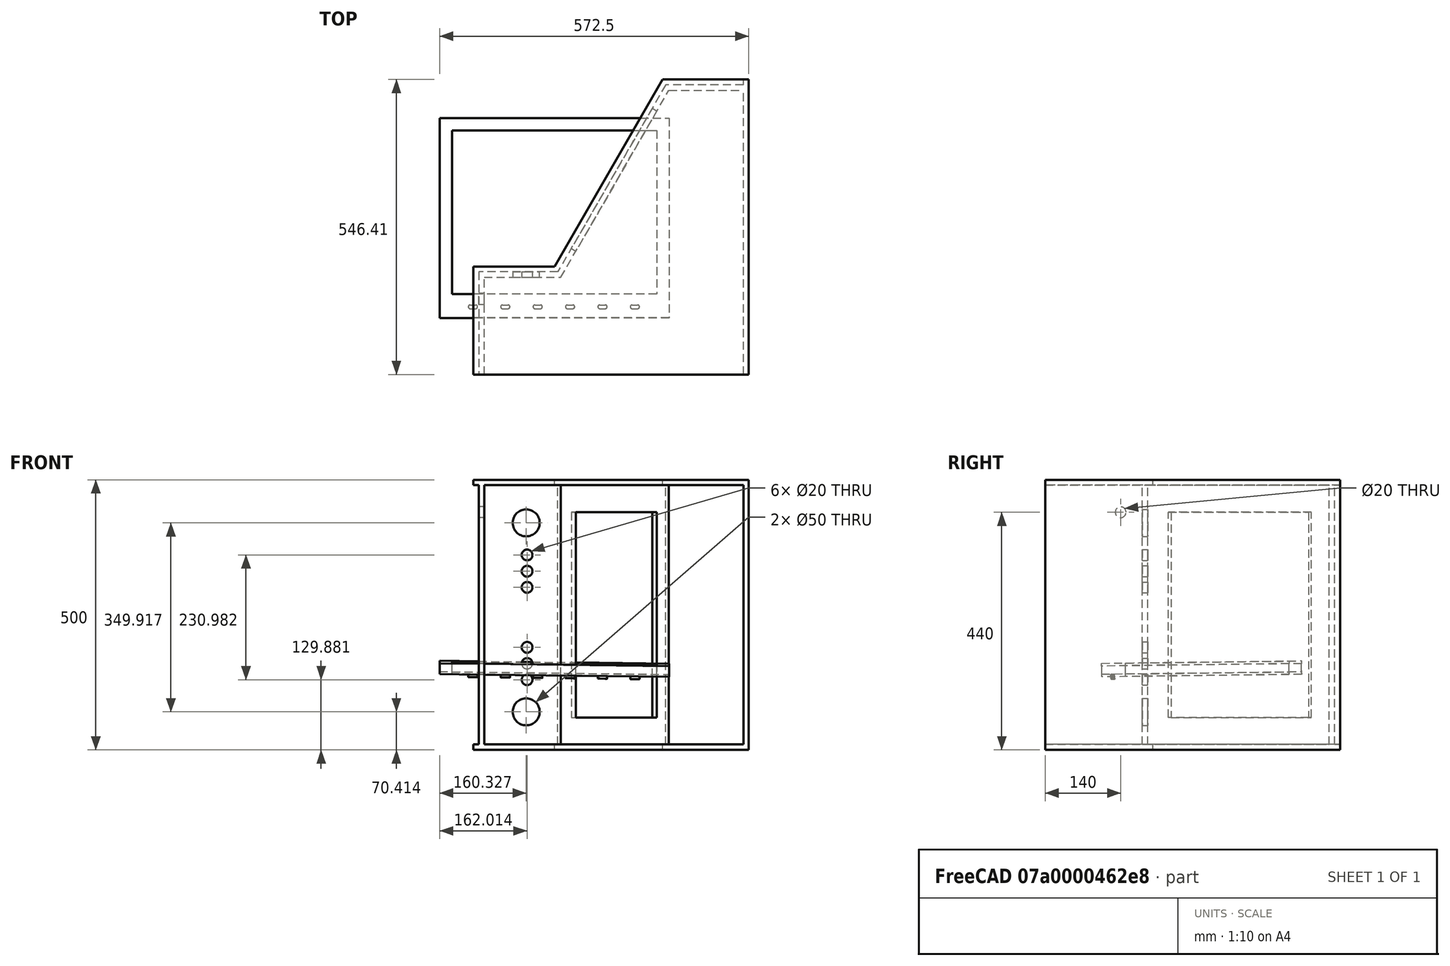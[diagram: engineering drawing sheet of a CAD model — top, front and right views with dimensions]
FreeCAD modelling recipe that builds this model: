
FCSTD DOCUMENT  (FreeCAD 0.18R16131 (Git))
Label: arcade
License: All rights reserved
LicenseURL: http://en.wikipedia.org/wiki/All_rights_reserved
objects: Sketcher::SketchObject×9, TechDraw::DrawViewDimension×7, PartDesign::Pad×5, PartDesign::Plane×3, PartDesign::Pocket×3, TechDraw::DrawViewPart×3, PartDesign::LinearPattern×2, PartDesign::Body×2, PartDesign::Mirrored×1, TechDraw::DrawSVGTemplate×1, TechDraw::DrawPage×1
note: 33 computed .brp shape members not serialized (recipe doc carries the construction recipe); baked Part::Feature solids carry a one-line shape summary decoded from their .brp

FEATURE [Sketcher::SketchObject] Sketch  label="coteGauche"
  MapMode = 5
  Support = -> [XY_Plane]
  sketch-geometry (6):
    g0: LineSegment StartX=-500 StartY=200 StartZ=0 EndX=-500 EndY=0 EndZ=0
    g1: LineSegment StartX=-500 StartY=0 StartZ=0 EndX=0 EndY=0 EndZ=0
    g2: LineSegment StartX=0 StartY=0 StartZ=0 EndX=0 EndY=546.41 EndZ=0
    g3: LineSegment StartX=0 StartY=546.41 StartZ=0 EndX=-149.507 EndY=546.41 EndZ=0
    g4: LineSegment StartX=-149.507 StartY=546.41 StartZ=0 EndX=-349.507 EndY=200 EndZ=0
    g5: LineSegment StartX=-349.507 StartY=200 StartZ=0 EndX=-500 EndY=200 EndZ=0
  constraints (16):
    c: Vertical(g0)
    c: Coincident(g0,g1)
    c: Horizontal(g1)
    c: Coincident(g1,g2)
    c: Vertical(g2)
    c: Coincident(g2,g3)
    c: Horizontal(g3)
    c: Coincident(g3,g4)
    c: Coincident(g5,g0)
    c: DistanceX(g1,g1) = 500
    c: DistanceY(g0,g0) = 200
    c: Horizontal(g5)
    c: Coincident(g4,g5)
    c: Coincident(g1,g-1)
    c: Angle(g4,g3) = 2.0944
    c: Distance(g4) = 400
FEATURE [PartDesign::Pad] Pad
  Length = 10
  Length2 = 100
  Profile = -> Sketch
  Type = 0
FEATURE [Sketcher::SketchObject] Sketch001
  ExternalGeometry = -> [Pad]
  MapMode = 5
  Placement = pos=(0,0,0) rot=(0.57735,0.57735,0.57735;2.0944rad)
  Support = -> [Pad]
  sketch-geometry (4):
    g0: LineSegment StartX=522.259 StartY=0 StartZ=0 EndX=-24.8181 EndY=0 EndZ=0
    g1: LineSegment StartX=-24.8181 StartY=0 StartZ=0 EndX=-24.8181 EndY=10 EndZ=0
    g2: LineSegment StartX=-24.8181 StartY=10 StartZ=0 EndX=522.259 EndY=10 EndZ=0
    g3: LineSegment StartX=522.259 StartY=10 StartZ=0 EndX=522.259 EndY=0 EndZ=0
  constraints (10):
    c: Coincident(g0,g1)
    c: Coincident(g1,g2)
    c: Coincident(g2,g3)
    c: Coincident(g3,g0)
    c: Horizontal(g0)
    c: Horizontal(g2)
    c: Vertical(g1)
    c: Vertical(g3)
    c: DistanceY(g0,g-3) = 10
    c: DistanceY(g-4,g2) = 10
FEATURE [Sketcher::SketchObject] Sketch002  label="arriere"
  ExternalGeometry = -> [Sketch]
  MapMode = 5
  Placement = pos=(0,0,0) rot=(0.57735,0.57735,0.57735;2.0944rad)
  Support = -> [YZ_Plane]
  sketch-geometry (4):
    g0: LineSegment StartX=0 StartY=0 StartZ=0 EndX=546.41 EndY=1.386e-13 EndZ=0
    g1: LineSegment StartX=546.41 StartY=1.386e-13 StartZ=0 EndX=546.41 EndY=500 EndZ=0
    g2: LineSegment StartX=546.41 StartY=500 StartZ=0 EndX=0 EndY=500 EndZ=0
    g3: LineSegment StartX=0 StartY=500 StartZ=0 EndX=0 EndY=0 EndZ=0
  constraints (10):
    c: Coincident(g0,g1)
    c: Coincident(g1,g2)
    c: Coincident(g2,g3)
    c: Coincident(g3,g0)
    c: Horizontal(g2)
    c: Vertical(g1)
    c: Vertical(g3)
    c: Coincident(g0,g-1)
    c: Coincident(g0,g-3)
    c: DistanceY(g1,g1) = 500
FEATURE [PartDesign::Pad] Pad001
  BaseFeature = -> Pad
  Length = 10
  Length2 = 100
  Profile = -> Sketch002
  Type = 0
FEATURE [PartDesign::LinearPattern] LinearPattern  label="coteDroit"
  BaseFeature = -> Pad001
  Direction = -> Z_Axis
  Length = 490
  Occurrences = 2
  Originals = -> [Pad]
FEATURE [Sketcher::SketchObject] Sketch003  label="Interieur"
  ExternalGeometry = -> [Sketch]
  MapMode = 5
  Support = -> [XY_Plane]
  sketch-geometry (14):
    g0: LineSegment StartX=-490 StartY=190 StartZ=0 EndX=-343.734 EndY=190 EndZ=0
    g1: LineSegment StartX=-343.734 StartY=190 StartZ=0 EndX=-143.734 EndY=536.41 EndZ=0
    g2: LineSegment StartX=-143.734 StartY=536.41 StartZ=0 EndX=0 EndY=536.41 EndZ=0
    g3: LineSegment StartX=0 StartY=536.41 StartZ=0 EndX=0 EndY=526.41 EndZ=0
    g4: LineSegment StartX=0 StartY=526.41 StartZ=0 EndX=-137.96 EndY=526.41 EndZ=0
    g5: LineSegment StartX=-137.96 StartY=526.41 StartZ=0 EndX=-337.96 EndY=180 EndZ=0
    g6: LineSegment StartX=-337.96 StartY=180 StartZ=0 EndX=-480 EndY=180 EndZ=0
    g7: LineSegment StartX=-480 StartY=180 StartZ=0 EndX=-480 EndY=0 EndZ=0
    g8: LineSegment StartX=-480 StartY=0 StartZ=0 EndX=-490 EndY=0 EndZ=0
    g9: LineSegment StartX=-490 StartY=0 StartZ=0 EndX=-490 EndY=190 EndZ=0
    g10: LineSegment [constr] StartX=-310.722 StartY=318.165 StartZ=0 EndX=-188.581 EndY=247.647 EndZ=0
    g11: GeomPoint X=-279.984 Y=300.419 Z=0
    g12: GeomPoint X=-271.323 Y=295.419 Z=0
    g13: GeomPoint X=-288.644 Y=305.419 Z=0
  constraints (37):
    c: Horizontal(g0)
    c: Coincident(g0,g1)
    c: Coincident(g1,g2)
    c: PointOnObject(g2,g-2)
    c: Horizontal(g2)
    c: Coincident(g2,g3)
    c: Coincident(g3,g4)
    c: Horizontal(g4)
    c: Coincident(g4,g5)
    c: Coincident(g5,g6)
    c: Horizontal(g6)
    c: Coincident(g6,g7)
    c: PointOnObject(g7,g-1)
    c: Vertical(g7)
    c: Coincident(g7,g8)
    c: PointOnObject(g8,g-1)
    c: Coincident(g8,g9)
    c: Vertical(g9)
    c: Coincident(g9,g0)
    c: DistanceX(g8,g7) = 10
    c: DistanceY(g6,g0) = 10
    c: Vertical(g3)
    c: DistanceY(g3,g2) = 10
    c: Parallel(g1,g5)
    c: Parallel(g-4,g1)
    c: DistanceY(g0,g-3) = 10
    c: DistanceY(g1,g-4) = 10
    c: Perpendicular(g5,g10)
    c: PointOnObject(g11,g1)
    c: PointOnObject(g12,g10)
    c: PointOnObject(g12,g5)
    c: PointOnObject(g11,g10)
    c: Distance(g11,g12) = 10
    c: PointOnObject(g13,g10)
    c: PointOnObject(g13,g-4)
    c: Distance(g13,g11) = 10
    c: DistanceX(g-3,g8) = 10
FEATURE [PartDesign::Pad] Pad002
  BaseFeature = -> LinearPattern
  Length = 490
  Length2 = 100
  Profile = -> Sketch003
  Type = 0
FEATURE [PartDesign::Plane] DatumPlane
  Length = 859.471
  MapMode = 5
  Placement = pos=(-340.073,196.341,0) rot=(-0.377964,0.654654,0.654654;3.86433rad)
  ResizeMode = 0
  Support = -> [Pad002]
  Width = 632.605
FEATURE [Sketcher::SketchObject] Sketch004  label="ecran"
  ExternalGeometry = -> [Pad002,Sketch003]
  MapMode = 5
  Placement = pos=(-340.073,196.341,0) rot=(-0.377964,0.654654,0.654654;3.86433rad)
  Support = -> [DatumPlane]
  sketch-geometry (5):
    g0: LineSegment StartX=-342.678 StartY=440 StartZ=0 EndX=-42.6779 EndY=440 EndZ=0
    g1: LineSegment StartX=-42.6779 StartY=440 StartZ=0 EndX=-42.6779 EndY=60 EndZ=0
    g2: LineSegment StartX=-42.6779 StartY=60 StartZ=0 EndX=-342.678 EndY=60 EndZ=0
    g3: LineSegment StartX=-342.678 StartY=60 StartZ=0 EndX=-342.678 EndY=440 EndZ=0
    g4: LineSegment [constr] StartX=7.32214 StartY=-5e-16 StartZ=0 EndX=7.32214 EndY=590 EndZ=0
  constraints (14):
    c: Coincident(g0,g1)
    c: Coincident(g1,g2)
    c: Coincident(g2,g3)
    c: Coincident(g3,g0)
    c: Horizontal(g0)
    c: Horizontal(g2)
    c: Vertical(g1)
    c: Vertical(g3)
    c: Distance(g0,g-5) = 50
    c: Distance(g1,g-7) = 50
    c: DistanceY(g0,g-5) = 50
    c: Coincident(g4,g-8)
    c: Vertical(g4)
    c: DistanceX(g1,g4) = 50
FEATURE [PartDesign::Pocket] Pocket
  BaseFeature = -> Pad002
  Length = 25
  Length2 = 100
  Profile = -> Sketch004
  Type = 0
FEATURE [PartDesign::Plane] DatumPlane001
  Length = 612
  MapMode = 5
  Placement = pos=(0,190,0) rot=(0,0.707107,0.707107;3.14159rad)
  ResizeMode = 0
  Support = -> [Pocket]
  Width = 612
FEATURE [Sketcher::SketchObject] Sketch005  label="manettes"
  ExternalGeometry = -> [Pocket]
  MapMode = 5
  Placement = pos=(0,190,0) rot=(0,0.707107,0.707107;3.14159rad)
  Support = -> [DatumPlane001]
  sketch-geometry (8):
    g0: LineSegment [constr] StartX=400.486 StartY=-101.961 StartZ=0 EndX=400.486 EndY=591.027 EndZ=0
    g1: LineSegment [constr] StartX=285.859 StartY=245.372 StartZ=0 EndX=534.194 EndY=245.372 EndZ=0
    g2: GeomPoint X=400.486 Y=10 Z=0
    g3: GeomPoint X=400.486 Y=490 Z=0
    g4: Circle CenterX=402.174 CenterY=70.4137 CenterZ=0 NormalX=0 NormalY=0 NormalZ=1 AngleXU=0 Radius=25
    g5: Circle CenterX=400.486 CenterY=129.881 CenterZ=0 NormalX=0 NormalY=0 NormalZ=1 AngleXU=0 Radius=10
    g6: Circle CenterX=400.486 CenterY=159.881 CenterZ=0 NormalX=0 NormalY=0 NormalZ=1 AngleXU=0 Radius=10
    g7: Circle CenterX=400.486 CenterY=189.881 CenterZ=0 NormalX=0 NormalY=0 NormalZ=1 AngleXU=0 Radius=10
  constraints (15):
    c: Vertical(g0)
    c: Horizontal(g1)
    c: PointOnObject(g2,g0)
    c: PointOnObject(g3,g0)
    c: PointOnObject(g2,g-5)
    c: PointOnObject(g3,g-6)
    c: Radius(g4) = 25
    c: PointOnObject(g5,g0)
    c: PointOnObject(g6,g0)
    c: PointOnObject(g7,g0)
    c: Radius(g5) = 10
    c: Radius(g6) = 10
    c: Radius(g7) = 10
    c: DistanceY(g5,g6) = 30
    c: DistanceY(g6,g7) = 30
FEATURE [PartDesign::Pocket] Pocket001
  BaseFeature = -> Pocket
  Length = 20
  Length2 = 100
  Profile = -> Sketch005
  Type = 1
FEATURE [PartDesign::Mirrored] Mirrored
  BaseFeature = -> Pocket001
  MirrorPlane = -> Sketch005 [Axis1]
  Originals = -> [Pocket001]
FEATURE [PartDesign::Plane] DatumPlane002
  Length = 662.95
  MapMode = 5
  Placement = pos=(-490,0,0) rot=(0.57735,-0.57735,-0.57735;2.0944rad)
  ResizeMode = 0
  Support = -> [Mirrored]
  Width = 616.54
FEATURE [Sketcher::SketchObject] Sketch006
  ExternalGeometry = -> [Mirrored]
  MapMode = 5
  Placement = pos=(-490,0,0) rot=(0.57735,-0.57735,-0.57735;2.0944rad)
  Support = -> [DatumPlane002]
  sketch-geometry (1):
    g0: Circle CenterX=-140 CenterY=440 CenterZ=0 NormalX=0 NormalY=0 NormalZ=1 AngleXU=0 Radius=10
  constraints (1):
    c: Radius(g0) = 10
FEATURE [PartDesign::Pocket] Pocket002
  BaseFeature = -> Mirrored
  Length = 20
  Length2 = 100
  Profile = -> Sketch006
  Type = 0
FEATURE [PartDesign::Body] Body  label="socle"
  Group = -> [Sketch,Pad,Sketch001,Sketch002,Pad001,LinearPattern,Sketch003,Pad002,DatumPlane,Sketch004,Pocket,DatumPlane001,Sketch005,Pocket001,Mirrored,DatumPlane002,Sketch006,Pocket002]
  Origin = -> Origin
  Tip = -> Pocket002
FEATURE [TechDraw::DrawSVGTemplate] Template
  EditableTexts = Designed_by_Name=Designed by Name; Drawing_number=Drawing number; FC-Date=Date; FC-SC=Scale; FC-SH=Sheet; FC-Title=Title; Subtitle=Subtitle; Weight=Weight
  Height = 210
  Orientation = 1
  Width = 297
FEATURE [TechDraw::DrawViewPart] View  label="3d"
  CoarseView = true
  Direction = (-0.678,0.458,0.575)
  Focus = 1000
  HardHidden = false
  IsoCount = 0
  IsoHidden = false
  IsoVisible = false
  LockPosition = false
  Perspective = false
  Rotation = 91
  Scale = 0.1
  ScaleType = 2
  SeamHidden = false
  SeamVisible = false
  SmoothHidden = false
  SmoothVisible = false
  Source = -> [Pocket002]
  X = 217.489
  Y = 140.455
FEATURE [TechDraw::DrawViewPart] View002  label="cote"
  CoarseView = false
  Direction = (0,0,1)
  Focus = 100
  HardHidden = false
  IsoCount = 0
  IsoHidden = false
  IsoVisible = false
  LockPosition = false
  Perspective = false
  Rotation = 0
  Scale = 0.1
  ScaleType = 2
  SeamHidden = false
  SeamVisible = false
  SmoothHidden = false
  SmoothVisible = false
  Source = -> [Pad]
  X = 52.6486
  Y = 136.95
FEATURE [TechDraw::DrawViewPart] View003  label="arriere001"
  CoarseView = false
  Direction = (1,0,0)
  Focus = 100
  HardHidden = false
  IsoCount = 0
  IsoHidden = false
  IsoVisible = false
  LockPosition = false
  Perspective = false
  Rotation = 0
  Scale = 0.1
  ScaleType = 0
  SeamHidden = false
  SeamVisible = false
  SmoothHidden = false
  SmoothVisible = false
  Source = -> [Pad001]
  X = 124.047
  Y = 136.884
FEATURE [TechDraw::DrawViewDimension] Dimension  label="profondeur"
  Arbitrary = false
  FormatSpec = %.2f
  LockPosition = false
  MeasureType = 1
  OverTolerance = 0.05
  References2D = -> [View002]
  Rotation = 0
  ScaleType = 0
  Type = 1
  UnderTolerance = 0
  X = 2.73693
  Y = -44.1616
FEATURE [TechDraw::DrawViewDimension] Dimension001  label="hauteur"
  Arbitrary = false
  FormatSpec = %.2f
  LockPosition = false
  MeasureType = 1
  OverTolerance = 0
  References2D = -> [View002]
  Rotation = 0
  ScaleType = 0
  Type = 2
  UnderTolerance = 0
  X = 29.57
  Y = -0.794788
FEATURE [TechDraw::DrawViewDimension] Dimension002
  Arbitrary = false
  FormatSpec = %.2f
  LockPosition = false
  MeasureType = 1
  OverTolerance = 0
  References2D = -> [View002]
  Rotation = 0
  ScaleType = 0
  Type = 2
  UnderTolerance = 0
  X = -34.7362
  Y = -12.8143
FEATURE [TechDraw::DrawViewDimension] Dimension003
  Arbitrary = false
  FormatSpec = %.2f
  LockPosition = false
  MeasureType = 1
  OverTolerance = 0
  References2D = -> [View002]
  Rotation = 0
  ScaleType = 0
  Type = 1
  UnderTolerance = 0
  X = -14.3386
  Y = 15.8632
FEATURE [TechDraw::DrawViewDimension] Dimension004  label="largeur"
  Arbitrary = false
  FormatSpec = %.2f
  LockPosition = false
  MeasureType = 1
  OverTolerance = 0
  References2D = -> [View003]
  Rotation = 0
  ScaleType = 0
  Type = 1
  UnderTolerance = 0
  X = -3.88903
  Y = -43.1793
FEATURE [TechDraw::DrawViewDimension] Dimension005
  Arbitrary = false
  FormatSpec = %.2f
  LockPosition = false
  MeasureType = 1
  OverTolerance = 0
  References2D = -> [View002]
  Rotation = 0
  ScaleType = 0
  Type = 1
  UnderTolerance = 0
  X = 20.3151
  Y = 38.9088
FEATURE [TechDraw::DrawViewDimension] Dimension006
  Arbitrary = false
  FormatSpec = %.2f
  LockPosition = false
  MeasureType = 0
  OverTolerance = 0
  References2D = -> [View]
  References3D = -> [Sketch]
  Rotation = 0
  ScaleType = 0
  Type = 0
  UnderTolerance = 0
  X = 38.925
  Y = -38.1835
FEATURE [TechDraw::DrawPage] Page
  KeepUpdated = true
  ProjectionType = 0
  Template = -> Template
  Views = -> [View,View002,View003,Dimension,Dimension001,Dimension002,Dimension003,Dimension004,Dimension005,Dimension006]
FEATURE [Sketcher::SketchObject] Sketch007
  MapMode = 5
  Support = -> [XY_Plane001]
  sketch-geometry (8):
    g0: LineSegment StartX=-212.5 StartY=185 StartZ=0 EndX=212.5 EndY=185 EndZ=0
    g1: LineSegment StartX=212.5 StartY=185 StartZ=0 EndX=212.5 EndY=-185 EndZ=0
    g2: LineSegment StartX=212.5 StartY=-185 StartZ=0 EndX=-212.5 EndY=-185 EndZ=0
    g3: LineSegment StartX=-212.5 StartY=-185 StartZ=0 EndX=-212.5 EndY=185 EndZ=0
    g4: LineSegment StartX=-189.5 StartY=162 StartZ=0 EndX=189.5 EndY=162 EndZ=0
    g5: LineSegment StartX=189.5 StartY=162 StartZ=0 EndX=189.5 EndY=-141 EndZ=0
    g6: LineSegment StartX=189.5 StartY=-141 StartZ=0 EndX=-189.5 EndY=-141 EndZ=0
    g7: LineSegment StartX=-189.5 StartY=-141 StartZ=0 EndX=-189.5 EndY=162 EndZ=0
  constraints (22):
    c: Coincident(g0,g1)
    c: Coincident(g1,g2)
    c: Coincident(g2,g3)
    c: Coincident(g3,g0)
    c: Horizontal(g2)
    c: Vertical(g1)
    c: Symmetric(g0,g0,g-2)
    c: Symmetric(g0,g2,g-1)
    c: DistanceY(g1,g0) = 370
    c: DistanceX(g0,g0) = 425
    c: Coincident(g4,g5)
    c: Coincident(g5,g6)
    c: Coincident(g6,g7)
    c: Coincident(g7,g4)
    c: Horizontal(g4)
    c: Horizontal(g6)
    c: Vertical(g5)
    c: Vertical(g7)
    c: DistanceY(g4,g0) = 23
    c: DistanceY(g2,g6) = 44
    c: DistanceX(g4,g0) = 23
    c: DistanceX(g0,g4) = 23
FEATURE [PartDesign::Pad] Pad003
  Length = 20
  Length2 = 100
  Profile = -> Sketch007
  Type = 0
FEATURE [Sketcher::SketchObject] Sketch008
  ExternalGeometry = -> [Sketch007]
  MapMode = 5
  Support = -> [XY_Plane001]
  sketch-geometry (5):
    g0: ArcOfCircle CenterX=-155.799 CenterY=-164.625 CenterZ=0 NormalX=0 NormalY=0 NormalZ=1 AngleXU=0 Radius=3.5 StartAngle=1.5708 EndAngle=4.71239
    g1: ArcOfCircle CenterX=-145.799 CenterY=-164.625 CenterZ=0 NormalX=0 NormalY=0 NormalZ=1 AngleXU=0 Radius=3.5 StartAngle=4.71239 EndAngle=7.85398
    g2: LineSegment StartX=-155.799 StartY=-168.125 StartZ=0 EndX=-145.799 EndY=-168.125 EndZ=0
    g3: LineSegment StartX=-155.799 StartY=-161.125 StartZ=0 EndX=-145.799 EndY=-161.125 EndZ=0
    g4: LineSegment [constr] StartX=-243.041 StartY=-164.625 StartZ=0 EndX=239.075 EndY=-164.625 EndZ=0
  constraints (10):
    c: Tangent(g0,g3) = 1.5708
    c: Tangent(g0,g2) = -1.5708
    c: Tangent(g2,g1) = -1.5708
    c: Tangent(g3,g1) = 1.5708
    c: Horizontal(g2)
    c: Equal(g0,g1)
    c: DistanceY(g0,g0) = 7
    c: DistanceX(g0,g1) = 10
    c: Horizontal(g4)
    c: PointOnObject(g1,g4)
FEATURE [PartDesign::Pad] Pad004  label="bouton"
  BaseFeature = -> Pad003
  Length = 5
  Length2 = 100
  Profile = -> Sketch008
  Reversed = true
  Type = 0
FEATURE [PartDesign::LinearPattern] LinearPattern001
  BaseFeature = -> Pad004
  Direction = -> Sketch008 [H_Axis]
  Length = 300
  Occurrences = 6
  Originals = -> [Pad004]
FEATURE [PartDesign::Body] Body001  label="Ecran"
  Group = -> [Sketch007,Pad003,Sketch008,Pad004,LinearPattern001]
  Origin = -> Origin001
  Placement = pos=(-350,290,140) rot=(0.707107,0.707107,0;0.017453rad)
  Tip = -> LinearPattern001
